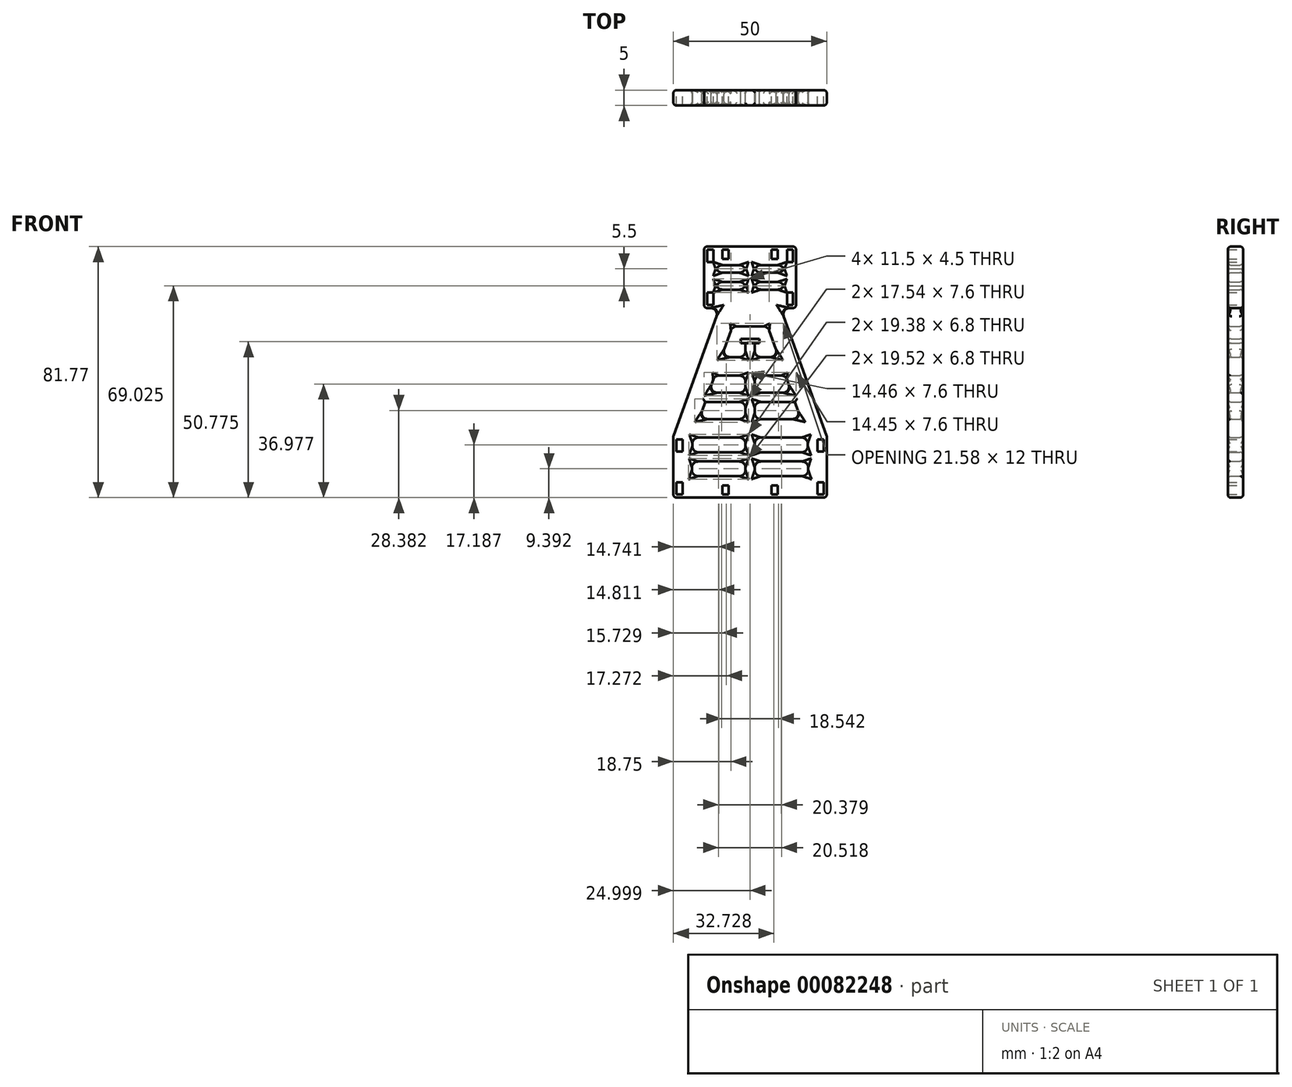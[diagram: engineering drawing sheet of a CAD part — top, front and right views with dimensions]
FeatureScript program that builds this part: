
annotation { "Feature Type Name" : "Feature", "Feature Type Description" : "" }
export const myFeature = defineFeature(function(context is Context, id is Id, definition is map)
    precondition{}
    {
        {
            var Q0;
            Q0=qCreatedBy(makeId("Front.planeOp"),FACE);
            var sketch = newSketch(context, id + "F0", { "sketchPlane" : qUnion([Q0])});
            skLineSegment(sketch, "E0", {"start": v(-24.3, -29.07) * mm, "end": v(-49.3, -29.07) * mm});
            skLineSegment(sketch, "E1", {"start": v(-24.3, -29.07) * mm, "end": v(0.7, -29.07) * mm});
            skLineSegment(sketch, "E2", {"start": v(-49.3, -29.07) * mm, "end": v(-49.3, -9.07) * mm});
            skLineSegment(sketch, "E3", {"start": v(0.7, -29.07) * mm, "end": v(0.7, -9.07) * mm});
            skLineSegment(sketch, "E4", {"start": v(-39.3, 52.7) * mm, "end": v(-39.3, 32.7) * mm});
            skLineSegment(sketch, "E5", {"start": v(-9.3, 52.7) * mm, "end": v(-9.3, 32.7) * mm});
            skLineSegment(sketch, "E6", {"start": v(-39.3, 32.7) * mm, "end": v(-34.3, 32.7) * mm});
            skLineSegment(sketch, "E7", {"start": v(-9.3, 32.7) * mm, "end": v(-14.3, 32.7) * mm});
            skLineSegment(sketch, "E8", {"start": v(-34.3, 32.7) * mm, "end": v(-49.3, -9.07) * mm});
            skLineSegment(sketch, "E9", {"start": v(-14.3, 32.7) * mm, "end": v(0.7, -9.07) * mm});
            skPoint(sketch, "E10.endSnap0", {"position": v(0.7, -19.07) * mm});
            skLineSegment(sketch, "E11", {"start": v(-49.3, -9.07) * mm, "end": v(-49.3, 32.7) * mm});
            skLineSegment(sketch, "E12", {"start": v(0.7, -9.07) * mm, "end": v(0.7, 32.7) * mm});
            skLineSegment(sketch, "E13", {"start": v(-49.3, 11.82) * mm, "end": v(-41.8, 11.82) * mm});
            skLineSegment(sketch, "E14", {"start": v(0.7, 11.82) * mm, "end": v(-6.8, 11.82) * mm});
            skLineSegment(sketch, "E15", {"start": v(-30.08, 26.7) * mm, "end": v(-18.52, 26.7) * mm});
            skLineSegment(sketch, "E16", {"start": v(-39.3, 52.7) * mm, "end": v(-9.3, 52.7) * mm});
            skLineSegment(sketch, "E17", {"start": v(-25.8, 16.7) * mm, "end": v(-25.8, 21.2) * mm});
            skLineSegment(sketch, "E18", {"start": v(-22.8, 16.7) * mm, "end": v(-22.8, 21.2) * mm});
            skLineSegment(sketch, "E19", {"start": v(-27.3, 21.2) * mm, "end": v(-25.8, 21.2) * mm});
            skLineSegment(sketch, "E20", {"start": v(-22.8, 21.2) * mm, "end": v(-21.3, 21.2) * mm});
            skLineSegment(sketch, "E21", {"start": v(-27.3, 21.2) * mm, "end": v(-27.3, 22.7) * mm});
            skLineSegment(sketch, "E22", {"start": v(-21.3, 21.2) * mm, "end": v(-21.3, 22.7) * mm});
            skLineSegment(sketch, "E23", {"start": v(-21.3, 22.7) * mm, "end": v(-27.3, 22.7) * mm});
            skLineSegment(sketch, "E24", {"start": v(-25.8, 10.7) * mm, "end": v(-35.83, 10.7) * mm});
            skLineSegment(sketch, "E25", {"start": v(-22.8, 10.7) * mm, "end": v(-12.78, 10.7) * mm});
            skLineSegment(sketch, "E26", {"start": v(-25.8, -3.49) * mm, "end": v(-40.92, -3.49) * mm});
            skLineSegment(sketch, "E27", {"start": v(-25.8, -9.49) * mm, "end": v(-43.08, -9.49) * mm});
            skLineSegment(sketch, "E28", {"start": v(-22.8, -3.49) * mm, "end": v(-7.68, -3.49) * mm});
            skLineSegment(sketch, "E29", {"start": v(-22.8, -9.49) * mm, "end": v(-5.53, -9.49) * mm});
            skLineSegment(sketch, "E30", {"start": v(-33.67, 16.7) * mm, "end": v(-30.08, 26.7) * mm});
            skLineSegment(sketch, "E31", {"start": v(-18.52, 26.7) * mm, "end": v(-14.93, 16.7) * mm});
            skLineSegment(sketch, "E32", {"start": v(-12.78, 10.7) * mm, "end": v(-7.68, -3.49) * mm});
            skLineSegment(sketch, "E33", {"start": v(-33.67, 16.7) * mm, "end": v(-25.8, 16.7) * mm});
            skLineSegment(sketch, "E34", {"start": v(-22.8, 16.7) * mm, "end": v(-14.93, 16.7) * mm});
            skLineSegment(sketch, "E35", {"start": v(-43.3, -22.08) * mm, "end": v(-25.8, -22.08) * mm});
            skLineSegment(sketch, "E36", {"start": v(-22.8, -22.08) * mm, "end": v(-5.3, -22.08) * mm});
            skLineSegment(sketch, "E37", {"start": v(-35.83, 10.7) * mm, "end": v(-37.83, 5.1) * mm});
            skLineSegment(sketch, "E38", {"start": v(-38.91, 2.1) * mm, "end": v(-40.92, -3.49) * mm});
            skLineSegment(sketch, "E39", {"start": v(-25.8, -3.49) * mm, "end": v(-25.8, 2.1) * mm});
            skLineSegment(sketch, "E40", {"start": v(-25.8, 5.1) * mm, "end": v(-25.8, 10.7) * mm});
            skLineSegment(sketch, "E41", {"start": v(-38.91, 2.1) * mm, "end": v(-25.8, 2.1) * mm});
            skLineSegment(sketch, "E42", {"start": v(-25.8, 5.1) * mm, "end": v(-37.83, 5.1) * mm});
            skLineSegment(sketch, "E43", {"start": v(-22.8, 2.1) * mm, "end": v(-9.69, 2.1) * mm});
            skLineSegment(sketch, "E44", {"start": v(-22.8, 5.1) * mm, "end": v(-10.77, 5.1) * mm});
            skLineSegment(sketch, "E45", {"start": v(-22.8, 10.7) * mm, "end": v(-22.8, 5.1) * mm});
            skLineSegment(sketch, "E46", {"start": v(-22.8, 2.1) * mm, "end": v(-22.8, -3.49) * mm});
            skLineSegment(sketch, "E47", {"start": v(-43.08, -9.49) * mm, "end": v(-43.16, -14.28) * mm});
            skLineSegment(sketch, "E48", {"start": v(-43.22, -17.28) * mm, "end": v(-43.3, -22.08) * mm});
            skLineSegment(sketch, "E49", {"start": v(-25.8, -17.28) * mm, "end": v(-25.8, -22.08) * mm});
            skLineSegment(sketch, "E50", {"start": v(-25.8, -9.49) * mm, "end": v(-25.8, -14.28) * mm});
            skLineSegment(sketch, "E51", {"start": v(-43.16, -14.28) * mm, "end": v(-25.8, -14.28) * mm});
            skLineSegment(sketch, "E52", {"start": v(-25.8, -17.28) * mm, "end": v(-43.22, -17.28) * mm});
            skLineSegment(sketch, "E53", {"start": v(-22.8, -14.28) * mm, "end": v(-5.44, -14.28) * mm});
            skLineSegment(sketch, "E54", {"start": v(-22.8, -17.28) * mm, "end": v(-5.39, -17.28) * mm});
            skLineSegment(sketch, "E55", {"start": v(-22.8, -9.49) * mm, "end": v(-22.8, -14.28) * mm});
            skLineSegment(sketch, "E56", {"start": v(-22.8, -17.28) * mm, "end": v(-22.8, -22.08) * mm});
            skLineSegment(sketch, "E57", {"start": v(-5.3, -22.08) * mm, "end": v(-5.39, -17.28) * mm});
            skLineSegment(sketch, "E58", {"start": v(-5.44, -14.28) * mm, "end": v(-5.53, -9.49) * mm});
            skLineSegment(sketch, "E59", {"start": v(-38.3, 51.7) * mm, "end": v(-36.3, 51.7) * mm});
            skLineSegment(sketch, "E60", {"start": v(-36.3, 33.7) * mm, "end": v(-38.3, 33.7) * mm});
            skLineSegment(sketch, "E61", {"start": v(-38.3, 47.7) * mm, "end": v(-36.3, 47.7) * mm});
            skLineSegment(sketch, "E62", {"start": v(-38.3, 37.7) * mm, "end": v(-36.3, 37.7) * mm});
            skLineSegment(sketch, "E63", {"start": v(-38.3, 51.7) * mm, "end": v(-38.3, 47.7) * mm});
            skLineSegment(sketch, "E64", {"start": v(-36.3, 51.7) * mm, "end": v(-36.3, 47.7) * mm});
            skLineSegment(sketch, "E65", {"start": v(-38.3, 37.7) * mm, "end": v(-38.3, 33.7) * mm});
            skLineSegment(sketch, "E66", {"start": v(-36.3, 37.7) * mm, "end": v(-36.3, 33.7) * mm});
            skLineSegment(sketch, "E67", {"start": v(-12.3, 51.7) * mm, "end": v(-10.3, 51.7) * mm});
            skLineSegment(sketch, "E68", {"start": v(-10.3, 33.7) * mm, "end": v(-12.3, 33.7) * mm});
            skLineSegment(sketch, "E69", {"start": v(-12.3, 47.7) * mm, "end": v(-10.3, 47.7) * mm});
            skLineSegment(sketch, "E70", {"start": v(-12.3, 37.7) * mm, "end": v(-10.3, 37.7) * mm});
            skLineSegment(sketch, "E71", {"start": v(-12.3, 51.7) * mm, "end": v(-12.3, 47.7) * mm});
            skLineSegment(sketch, "E72", {"start": v(-10.3, 51.7) * mm, "end": v(-10.3, 47.7) * mm});
            skLineSegment(sketch, "E73", {"start": v(-12.3, 37.7) * mm, "end": v(-12.3, 33.7) * mm});
            skLineSegment(sketch, "E74", {"start": v(-10.3, 37.7) * mm, "end": v(-10.3, 33.7) * mm});
            skLineSegment(sketch, "E75", {"start": v(-34.3, 32.7) * mm, "end": v(-14.3, 32.7) * mm});
            skLineSegment(sketch, "E76", {"start": v(-35.3, 44.2) * mm, "end": v(-25.8, 44.2) * mm});
            skLineSegment(sketch, "E77", {"start": v(-35.3, 41.2) * mm, "end": v(-25.8, 41.2) * mm});
            skLineSegment(sketch, "E78", {"start": v(-35.3, 46.7) * mm, "end": v(-35.3, 44.2) * mm});
            skLineSegment(sketch, "E79", {"start": v(-35.3, 41.2) * mm, "end": v(-35.3, 38.7) * mm});
            skLineSegment(sketch, "E80", {"start": v(-22.8, 44.2) * mm, "end": v(-13.3, 44.2) * mm});
            skLineSegment(sketch, "E81", {"start": v(-22.8, 41.2) * mm, "end": v(-13.3, 41.2) * mm});
            skLineSegment(sketch, "E82", {"start": v(-35.3, 38.7) * mm, "end": v(-25.8, 38.7) * mm});
            skLineSegment(sketch, "E83", {"start": v(-22.8, 38.7) * mm, "end": v(-13.3, 38.7) * mm});
            skLineSegment(sketch, "E84", {"start": v(-13.3, 46.7) * mm, "end": v(-13.3, 44.2) * mm});
            skLineSegment(sketch, "E85", {"start": v(-13.3, 41.2) * mm, "end": v(-13.3, 38.7) * mm});
            skLineSegment(sketch, "E86", {"start": v(-25.8, 41.2) * mm, "end": v(-25.8, 38.7) * mm});
            skLineSegment(sketch, "E87", {"start": v(-22.8, 41.2) * mm, "end": v(-22.8, 38.7) * mm});
            skLineSegment(sketch, "E88", {"start": v(-25.8, 44.2) * mm, "end": v(-25.8, 46.7) * mm});
            skLineSegment(sketch, "E89", {"start": v(-22.8, 44.2) * mm, "end": v(-22.8, 46.7) * mm});
            skLineSegment(sketch, "E90", {"start": v(-35.3, 46.7) * mm, "end": v(-25.8, 46.7) * mm});
            skLineSegment(sketch, "E91", {"start": v(-22.8, 46.7) * mm, "end": v(-13.3, 46.7) * mm});
            skLineSegment(sketch, "E92", {"start": v(-48.3, -28.07) * mm, "end": v(-46.3, -28.07) * mm});
            skLineSegment(sketch, "E93", {"start": v(-46.3, -10.07) * mm, "end": v(-48.3, -10.07) * mm});
            skLineSegment(sketch, "E94", {"start": v(-48.3, -24.07) * mm, "end": v(-46.3, -24.07) * mm});
            skLineSegment(sketch, "E95", {"start": v(-46.3, -14.07) * mm, "end": v(-48.3, -14.07) * mm});
            skLineSegment(sketch, "E96", {"start": v(-48.3, -10.07) * mm, "end": v(-48.3, -14.07) * mm});
            skLineSegment(sketch, "E97", {"start": v(-46.3, -10.07) * mm, "end": v(-46.3, -14.07) * mm});
            skLineSegment(sketch, "E98", {"start": v(-48.3, -24.07) * mm, "end": v(-48.3, -28.07) * mm});
            skLineSegment(sketch, "E99", {"start": v(-46.3, -24.07) * mm, "end": v(-46.3, -28.07) * mm});
            skLineSegment(sketch, "E100", {"start": v(-0.3, -28.07) * mm, "end": v(-2.3, -28.07) * mm});
            skLineSegment(sketch, "E101", {"start": v(-2.3, -24.07) * mm, "end": v(-2.3, -28.07) * mm});
            skLineSegment(sketch, "E102", {"start": v(-2.3, -24.07) * mm, "end": v(-0.3, -24.07) * mm});
            skLineSegment(sketch, "E103", {"start": v(-0.3, -10.07) * mm, "end": v(-2.3, -10.07) * mm});
            skLineSegment(sketch, "E104", {"start": v(-0.3, -14.07) * mm, "end": v(-2.3, -14.07) * mm});
            skLineSegment(sketch, "E105", {"start": v(-2.3, -14.07) * mm, "end": v(-2.3, -10.07) * mm});
            skLineSegment(sketch, "E106", {"start": v(-0.3, -10.07) * mm, "end": v(-0.3, -14.07) * mm});
            skLineSegment(sketch, "E107", {"start": v(-0.3, -24.07) * mm, "end": v(-0.3, -28.07) * mm});
            skLineSegment(sketch, "E108", {"start": v(-33.3, 51.7) * mm, "end": v(-33.3, 48.7) * mm});
            skLineSegment(sketch, "E109", {"start": v(-33.3, 51.7) * mm, "end": v(-31.3, 51.7) * mm});
            skLineSegment(sketch, "E110", {"start": v(-31.3, 51.7) * mm, "end": v(-31.3, 48.7) * mm});
            skLineSegment(sketch, "E111", {"start": v(-31.3, 48.7) * mm, "end": v(-33.33, 48.71) * mm});
            skLineSegment(sketch, "E112", {"start": v(-15.3, 51.7) * mm, "end": v(-15.3, 48.7) * mm});
            skLineSegment(sketch, "E113", {"start": v(-15.3, 48.7) * mm, "end": v(-17.3, 48.7) * mm});
            skLineSegment(sketch, "E114", {"start": v(-17.3, 48.7) * mm, "end": v(-17.3, 51.7) * mm});
            skLineSegment(sketch, "E115", {"start": v(-17.3, 51.7) * mm, "end": v(-15.3, 51.7) * mm});
            skLineSegment(sketch, "E116", {"start": v(-33.3, -28.07) * mm, "end": v(-31.3, -28.07) * mm});
            skLineSegment(sketch, "E117", {"start": v(-31.3, -28.07) * mm, "end": v(-31.3, -25.07) * mm});
            skLineSegment(sketch, "E118", {"start": v(-31.3, -25.07) * mm, "end": v(-33.3, -25.07) * mm});
            skLineSegment(sketch, "E119", {"start": v(-33.3, -25.07) * mm, "end": v(-33.3, -28.07) * mm});
            skLineSegment(sketch, "E120", {"start": v(-15.3, -28.07) * mm, "end": v(-17.3, -28.07) * mm});
            skLineSegment(sketch, "E121", {"start": v(-17.3, -28.07) * mm, "end": v(-17.3, -25.07) * mm});
            skLineSegment(sketch, "E122", {"start": v(-17.3, -25.07) * mm, "end": v(-15.3, -25.07) * mm});
            skLineSegment(sketch, "E123", {"start": v(-15.3, -25.07) * mm, "end": v(-15.3, -28.07) * mm});
            skLineSegment(sketch, "E124", {"start": v(-46.3, -28.07) * mm, "end": v(-33.3, -28.07) * mm});
            skLineSegment(sketch, "E125", {"start": v(-15.3, -28.07) * mm, "end": v(-2.3, -28.07) * mm});
            skLineSegment(sketch, "E126", {"start": v(-36.3, 51.7) * mm, "end": v(-33.3, 51.7) * mm});
            skLineSegment(sketch, "E127", {"start": v(-15.3, 51.7) * mm, "end": v(-12.3, 51.7) * mm});
            skLineSegment(sketch, "E128", {"start": v(-17.3, -28.07) * mm, "end": v(-31.3, -28.07) * mm});
            skSolve(sketch);
        }
        {
            var Q0;
            Q0=makeQuery(id+"F0.imprint","IMPRINT",FACE,{"disambiguationData":[TD([[makeQuery(id+"F0.imprint","IMPRINT",EDGE,{"derivedFrom":sQuery(id+"F0.wireOp",EDGE,"E0")}),-1.0]])]});
            var Q1;
            {var subQ0=sQuery(id+"F0.wireOp",EDGE,"Gmn1fpuc-x4fh-Dt10-x9JC-7DTWN6bsxrZ6");var subQ3=sQuery(id+"F0.wireOp",EDGE,"DaSBLwFQ-kMCm-d5nd-0PkE-b7sn5duXBcw0");var subQ4=makeQuery(id+"F0.imprint","INTERSECT",VERTEX,{"derivedFrom":[subQ3,subQ0]});Q1=makeQuery(id+"F0.imprint","IMPRINT",FACE,{"disambiguationData":[TD([[makeQuery(id+"F0.imprint","IMPRINT",EDGE,{"disambiguationData":[TD([[subQ4,1.0]])],"derivedFrom":subQ3}),-1.0]])]});}
            var Q2;
            {var subQ0=sQuery(id+"F0.wireOp",EDGE,"E17");Q2=makeQuery(id+"F0.imprint","IMPRINT",FACE,{"disambiguationData":[TD([[makeQuery(id+"F0.imprint","IMPRINT",EDGE,{"derivedFrom":subQ0}),-1.0]])]});}
            var Q3;
            {var subQ0=sQuery(id+"F0.wireOp",EDGE,"Cksz0ew8-7FD8-2HIo-WUUZ-xffdrkzJC516");Q3=makeQuery(id+"F0.imprint","IMPRINT",FACE,{"disambiguationData":[TD([[makeQuery(id+"F0.imprint","IMPRINT",EDGE,{"derivedFrom":subQ0}),-1.0]])]});}
            var Q4;
            {var subQ0=sQuery(id+"F0.wireOp",EDGE,"r91MVb0x-F113-lwMS-o9z4-GQMOX2XZy89u");var subQ3=makeQuery(id+"F0.imprint","INTERSECT",VERTEX,{"derivedFrom":[subQ0,sQuery(id+"F0.wireOp",EDGE,"uLksvqQd-syN0-xw4T-CYru-WyKsU3DyxEXD")]});Q4=makeQuery(id+"F0.imprint","IMPRINT",FACE,{"disambiguationData":[TD([[makeQuery(id+"F0.imprint","IMPRINT",EDGE,{"disambiguationData":[TD([[subQ3,-1.0]])],"derivedFrom":subQ0}),1.0]])]});}
            var Q5;
            {var subQ0=sQuery(id+"F0.wireOp",EDGE,"uLksvqQd-syN0-xw4T-CYru-WyKsU3DyxEXD");Q5=makeQuery(id+"F0.imprint","IMPRINT",FACE,{"disambiguationData":[TD([[makeQuery(id+"F0.imprint","IMPRINT",EDGE,{"derivedFrom":subQ0}),-1.0]])]});}
            var Q6;
            {var subQ0=sQuery(id+"F0.wireOp",EDGE,"E4");Q6=makeQuery(id+"F0.imprint","IMPRINT",FACE,{"disambiguationData":[TD([[makeQuery(id+"F0.imprint","IMPRINT",EDGE,{"derivedFrom":subQ0}),1.0]])]});}
            var Q7;
            {var subQ5=sQuery(id+"F0.wireOp",EDGE,"wKnZqxov-nZ8u-8Se3-picp-5adwDS9QqPhn");Q7=makeQuery(id+"F0.imprint","IMPRINT",FACE,{"disambiguationData":[TD([[makeQuery(id+"F0.imprint","IMPRINT",EDGE,{"derivedFrom":subQ5}),1.0]])]});}
            var Q8;
            {var subQ1=sQuery(id+"F0.wireOp",EDGE,"E5");Q8=makeQuery(id+"F0.imprint","IMPRINT",FACE,{"disambiguationData":[TD([[makeQuery(id+"F0.imprint","IMPRINT",EDGE,{"derivedFrom":subQ1}),-1.0]])]});}
            extrude(context, id + "F1", {"entities" : qUnion([Q0, Q1, Q2, Q3, Q4, Q5, Q6, Q7, Q8]), "depth" : 5 * mm});
        }
        {
            var Q0;
            Q0=makeQuery(id+"F1.opExtrude","CAP_EDGE",EDGE,{"disambiguationData":[OSD([sQuery(id+"F0.wireOp",EDGE,"E2")])],"isStart":false});
            var Q1;
            Q1=makeQuery(id+"F1.opExtrude","CAP_EDGE",EDGE,{"disambiguationData":[OSD([sQuery(id+"F0.wireOp",EDGE,"E0"),sQuery(id+"F0.wireOp",EDGE,"E1")])],"isStart":false});
            var Q2;
            Q2=makeQuery(id+"F1.opExtrude","CAP_EDGE",EDGE,{"disambiguationData":[OSD([sQuery(id+"F0.wireOp",EDGE,"E8")])],"isStart":false});
            var Q3;
            Q3=makeQuery(id+"F1.opExtrude","CAP_EDGE",EDGE,{"disambiguationData":[OSD([sQuery(id+"F0.wireOp",EDGE,"E3")])],"isStart":false});
            var Q4;
            Q4=makeQuery(id+"F1.opExtrude","CAP_EDGE",EDGE,{"disambiguationData":[OSD([sQuery(id+"F0.wireOp",EDGE,"E9")])],"isStart":false});
            var Q5;
            Q5=makeQuery(id+"F1.opExtrude","CAP_EDGE",EDGE,{"disambiguationData":[OSD([sQuery(id+"F0.wireOp",EDGE,"E51")])],"isStart":false});
            var Q6;
            Q6=makeQuery(id+"F1.opExtrude","CAP_EDGE",EDGE,{"disambiguationData":[OSD([sQuery(id+"F0.wireOp",EDGE,"E52")])],"isStart":false});
            var Q7;
            Q7=makeQuery(id+"F1.opExtrude","CAP_EDGE",EDGE,{"disambiguationData":[OSD([sQuery(id+"F0.wireOp",EDGE,"E48")])],"isStart":false});
            var Q8;
            Q8=makeQuery(id+"F1.opExtrude","CAP_EDGE",EDGE,{"disambiguationData":[OSD([sQuery(id+"F0.wireOp",EDGE,"E47")])],"isStart":false});
            var Q9;
            Q9=makeQuery(id+"F1.opExtrude","CAP_EDGE",EDGE,{"disambiguationData":[OSD([sQuery(id+"F0.wireOp",EDGE,"E27")])],"isStart":false});
            var Q10;
            Q10=makeQuery(id+"F1.opExtrude","CAP_EDGE",EDGE,{"disambiguationData":[OSD([sQuery(id+"F0.wireOp",EDGE,"E50")])],"isStart":false});
            var Q11;
            Q11=makeQuery(id+"F1.opExtrude","CAP_EDGE",EDGE,{"disambiguationData":[OSD([sQuery(id+"F0.wireOp",EDGE,"E35")])],"isStart":false});
            var Q12;
            Q12=makeQuery(id+"F1.opExtrude","CAP_EDGE",EDGE,{"disambiguationData":[OSD([sQuery(id+"F0.wireOp",EDGE,"E49")])],"isStart":false});
            var Q13;
            Q13=makeQuery(id+"F1.opExtrude","CAP_EDGE",EDGE,{"disambiguationData":[OSD([sQuery(id+"F0.wireOp",EDGE,"E36")])],"isStart":false});
            var Q14;
            Q14=makeQuery(id+"F1.opExtrude","CAP_EDGE",EDGE,{"disambiguationData":[OSD([sQuery(id+"F0.wireOp",EDGE,"E56")])],"isStart":false});
            var Q15;
            Q15=makeQuery(id+"F1.opExtrude","CAP_EDGE",EDGE,{"disambiguationData":[OSD([sQuery(id+"F0.wireOp",EDGE,"E54")])],"isStart":false});
            var Q16;
            Q16=makeQuery(id+"F1.opExtrude","CAP_EDGE",EDGE,{"disambiguationData":[OSD([sQuery(id+"F0.wireOp",EDGE,"E57")])],"isStart":false});
            var Q17;
            Q17=makeQuery(id+"F1.opExtrude","CAP_EDGE",EDGE,{"disambiguationData":[OSD([sQuery(id+"F0.wireOp",EDGE,"E29")])],"isStart":false});
            var Q18;
            Q18=makeQuery(id+"F1.opExtrude","CAP_EDGE",EDGE,{"disambiguationData":[OSD([sQuery(id+"F0.wireOp",EDGE,"E55")])],"isStart":false});
            var Q19;
            Q19=makeQuery(id+"F1.opExtrude","CAP_EDGE",EDGE,{"disambiguationData":[OSD([sQuery(id+"F0.wireOp",EDGE,"E58")])],"isStart":false});
            var Q20;
            Q20=makeQuery(id+"F1.opExtrude","CAP_EDGE",EDGE,{"disambiguationData":[OSD([sQuery(id+"F0.wireOp",EDGE,"E38")])],"isStart":false});
            var Q21;
            Q21=makeQuery(id+"F1.opExtrude","CAP_EDGE",EDGE,{"disambiguationData":[OSD([sQuery(id+"F0.wireOp",EDGE,"E26")])],"isStart":false});
            var Q22;
            Q22=makeQuery(id+"F1.opExtrude","CAP_EDGE",EDGE,{"disambiguationData":[OSD([sQuery(id+"F0.wireOp",EDGE,"E41")])],"isStart":false});
            var Q23;
            Q23=makeQuery(id+"F1.opExtrude","CAP_EDGE",EDGE,{"disambiguationData":[OSD([sQuery(id+"F0.wireOp",EDGE,"E39")])],"isStart":false});
            var Q24;
            Q24=makeQuery(id+"F1.opExtrude","CAP_EDGE",EDGE,{"disambiguationData":[OSD([sQuery(id+"F0.wireOp",EDGE,"E46")])],"isStart":false});
            var Q25;
            Q25=makeQuery(id+"F1.opExtrude","CAP_EDGE",EDGE,{"disambiguationData":[OSD([sQuery(id+"F0.wireOp",EDGE,"E43")])],"isStart":false});
            var Q26;
            {var subQ0=sQuery(id+"F0.wireOp",EDGE,"E32");Q26=makeQuery(id+"F1.opExtrude","CAP_EDGE",EDGE,{"disambiguationData":[OSD([subQ0]),TDD([makeQuery(id+"F0.imprint","IMPRINT",EDGE,{"disambiguationData":[TD([[makeQuery(id+"F0.imprint","INTERSECT",VERTEX,{"derivedFrom":[sQuery(id+"F0.wireOp",EDGE,"E28"),subQ0]}),1.0]])],"derivedFrom":subQ0})])],"isStart":false});}
            var Q27;
            Q27=makeQuery(id+"F1.opExtrude","CAP_EDGE",EDGE,{"disambiguationData":[OSD([sQuery(id+"F0.wireOp",EDGE,"E28")])],"isStart":false});
            var Q28;
            Q28=makeQuery(id+"F1.opExtrude","CAP_EDGE",EDGE,{"disambiguationData":[OSD([sQuery(id+"F0.wireOp",EDGE,"E45")])],"isStart":false});
            var Q29;
            Q29=makeQuery(id+"F1.opExtrude","CAP_EDGE",EDGE,{"disambiguationData":[OSD([sQuery(id+"F0.wireOp",EDGE,"E44")])],"isStart":false});
            var Q30;
            Q30=makeQuery(id+"F1.opExtrude","CAP_EDGE",EDGE,{"disambiguationData":[OSD([sQuery(id+"F0.wireOp",EDGE,"E25")])],"isStart":false});
            var Q31;
            {var subQ0=sQuery(id+"F0.wireOp",EDGE,"E32");Q31=makeQuery(id+"F1.opExtrude","CAP_EDGE",EDGE,{"disambiguationData":[OSD([subQ0]),TDD([makeQuery(id+"F0.imprint","IMPRINT",EDGE,{"disambiguationData":[TD([[makeQuery(id+"F0.imprint","INTERSECT",VERTEX,{"derivedFrom":[sQuery(id+"F0.wireOp",EDGE,"E25"),subQ0]}),-1.0]])],"derivedFrom":subQ0})])],"isStart":false});}
            var Q32;
            Q32=makeQuery(id+"F1.opExtrude","CAP_EDGE",EDGE,{"disambiguationData":[OSD([sQuery(id+"F0.wireOp",EDGE,"E42")])],"isStart":false});
            var Q33;
            Q33=makeQuery(id+"F1.opExtrude","CAP_EDGE",EDGE,{"disambiguationData":[OSD([sQuery(id+"F0.wireOp",EDGE,"E37")])],"isStart":false});
            var Q34;
            Q34=makeQuery(id+"F1.opExtrude","CAP_EDGE",EDGE,{"disambiguationData":[OSD([sQuery(id+"F0.wireOp",EDGE,"E24")])],"isStart":false});
            var Q35;
            Q35=makeQuery(id+"F1.opExtrude","CAP_EDGE",EDGE,{"disambiguationData":[OSD([sQuery(id+"F0.wireOp",EDGE,"E40")])],"isStart":false});
            var Q36;
            Q36=makeQuery(id+"F1.opExtrude","CAP_EDGE",EDGE,{"disambiguationData":[OSD([sQuery(id+"F0.wireOp",EDGE,"E33")])],"isStart":false});
            var Q37;
            Q37=makeQuery(id+"F1.opExtrude","CAP_EDGE",EDGE,{"disambiguationData":[OSD([sQuery(id+"F0.wireOp",EDGE,"E30")])],"isStart":false});
            var Q38;
            Q38=makeQuery(id+"F1.opExtrude","CAP_EDGE",EDGE,{"disambiguationData":[OSD([sQuery(id+"F0.wireOp",EDGE,"E15")])],"isStart":false});
            var Q39;
            Q39=makeQuery(id+"F1.opExtrude","CAP_EDGE",EDGE,{"disambiguationData":[OSD([sQuery(id+"F0.wireOp",EDGE,"E31")])],"isStart":false});
            var Q40;
            Q40=makeQuery(id+"F1.opExtrude","CAP_EDGE",EDGE,{"disambiguationData":[OSD([sQuery(id+"F0.wireOp",EDGE,"E34")])],"isStart":false});
            var Q41;
            Q41=makeQuery(id+"F1.opExtrude","CAP_EDGE",EDGE,{"disambiguationData":[OSD([sQuery(id+"F0.wireOp",EDGE,"E17")])],"isStart":false});
            var Q42;
            Q42=makeQuery(id+"F1.opExtrude","CAP_EDGE",EDGE,{"disambiguationData":[OSD([sQuery(id+"F0.wireOp",EDGE,"E18")])],"isStart":false});
            var Q43;
            Q43=makeQuery(id+"F1.opExtrude","CAP_EDGE",EDGE,{"disambiguationData":[OSD([sQuery(id+"F0.wireOp",EDGE,"E6")])],"isStart":false});
            var Q44;
            Q44=makeQuery(id+"F1.opExtrude","CAP_EDGE",EDGE,{"disambiguationData":[OSD([sQuery(id+"F0.wireOp",EDGE,"E4")])],"isStart":false});
            var Q45;
            Q45=makeQuery(id+"F1.opExtrude","CAP_EDGE",EDGE,{"disambiguationData":[OSD([sQuery(id+"F0.wireOp",EDGE,"E16")])],"isStart":false});
            var Q46;
            Q46=makeQuery(id+"F1.opExtrude","CAP_EDGE",EDGE,{"disambiguationData":[OSD([sQuery(id+"F0.wireOp",EDGE,"E5")])],"isStart":false});
            var Q47;
            Q47=makeQuery(id+"F1.opExtrude","CAP_EDGE",EDGE,{"disambiguationData":[OSD([sQuery(id+"F0.wireOp",EDGE,"E7")])],"isStart":false});
            var Q48;
            Q48=makeQuery(id+"F1.opExtrude","CAP_EDGE",EDGE,{"disambiguationData":[OSD([sQuery(id+"F0.wireOp",EDGE,"ymKoGDRe-bliB-sY5n-xFfI-t996A0unm5Td")])],"isStart":false});
            var Q49;
            Q49=makeQuery(id+"F1.opExtrude","CAP_EDGE",EDGE,{"disambiguationData":[OSD([sQuery(id+"F0.wireOp",EDGE,"wKnZqxov-nZ8u-8Se3-picp-5adwDS9QqPhn")])],"isStart":false});
            var Q50;
            Q50=makeQuery(id+"F1.opExtrude","CAP_EDGE",EDGE,{"disambiguationData":[OSD([sQuery(id+"F0.wireOp",EDGE,"p78FREQm-4KwS-vw5M-QSKw-gRrmDGhDhAHL")])],"isStart":false});
            var Q51;
            Q51=makeQuery(id+"F1.opExtrude","CAP_EDGE",EDGE,{"disambiguationData":[OSD([sQuery(id+"F0.wireOp",EDGE,"E76")])],"isStart":false});
            var Q52;
            Q52=makeQuery(id+"F1.opExtrude","CAP_EDGE",EDGE,{"disambiguationData":[OSD([sQuery(id+"F0.wireOp",EDGE,"E78")])],"isStart":false});
            var Q53;
            Q53=makeQuery(id+"F1.opExtrude","CAP_EDGE",EDGE,{"disambiguationData":[OSD([sQuery(id+"F0.wireOp",EDGE,"E90")])],"isStart":false});
            var Q54;
            Q54=makeQuery(id+"F1.opExtrude","CAP_EDGE",EDGE,{"disambiguationData":[OSD([sQuery(id+"F0.wireOp",EDGE,"E88")])],"isStart":false});
            var Q55;
            Q55=makeQuery(id+"F1.opExtrude","CAP_EDGE",EDGE,{"disambiguationData":[OSD([sQuery(id+"F0.wireOp",EDGE,"E80")])],"isStart":false});
            var Q56;
            Q56=makeQuery(id+"F1.opExtrude","CAP_EDGE",EDGE,{"disambiguationData":[OSD([sQuery(id+"F0.wireOp",EDGE,"E91")])],"isStart":false});
            var Q57;
            Q57=makeQuery(id+"F1.opExtrude","CAP_EDGE",EDGE,{"disambiguationData":[OSD([sQuery(id+"F0.wireOp",EDGE,"E89")])],"isStart":false});
            var Q58;
            Q58=makeQuery(id+"F1.opExtrude","CAP_EDGE",EDGE,{"disambiguationData":[OSD([sQuery(id+"F0.wireOp",EDGE,"E84")])],"isStart":false});
            var Q59;
            Q59=makeQuery(id+"F1.opExtrude","CAP_EDGE",EDGE,{"disambiguationData":[OSD([sQuery(id+"F0.wireOp",EDGE,"E87")])],"isStart":false});
            var Q60;
            Q60=makeQuery(id+"F1.opExtrude","CAP_EDGE",EDGE,{"disambiguationData":[OSD([sQuery(id+"F0.wireOp",EDGE,"E81")])],"isStart":false});
            var Q61;
            Q61=makeQuery(id+"F1.opExtrude","CAP_EDGE",EDGE,{"disambiguationData":[OSD([sQuery(id+"F0.wireOp",EDGE,"E85")])],"isStart":false});
            var Q62;
            Q62=makeQuery(id+"F1.opExtrude","CAP_EDGE",EDGE,{"disambiguationData":[OSD([sQuery(id+"F0.wireOp",EDGE,"E83")])],"isStart":false});
            var Q63;
            Q63=makeQuery(id+"F1.opExtrude","CAP_EDGE",EDGE,{"disambiguationData":[OSD([sQuery(id+"F0.wireOp",EDGE,"E77")])],"isStart":false});
            var Q64;
            Q64=makeQuery(id+"F1.opExtrude","CAP_EDGE",EDGE,{"disambiguationData":[OSD([sQuery(id+"F0.wireOp",EDGE,"E79")])],"isStart":false});
            var Q65;
            Q65=makeQuery(id+"F1.opExtrude","CAP_EDGE",EDGE,{"disambiguationData":[OSD([sQuery(id+"F0.wireOp",EDGE,"E82")])],"isStart":false});
            var Q66;
            Q66=makeQuery(id+"F1.opExtrude","CAP_EDGE",EDGE,{"disambiguationData":[OSD([sQuery(id+"F0.wireOp",EDGE,"E86")])],"isStart":false});
            var Q67;
            Q67=makeQuery(id+"F1.opExtrude","CAP_EDGE",EDGE,{"disambiguationData":[OSD([sQuery(id+"F0.wireOp",EDGE,"E53")])],"isStart":false});
            var Q68;
            Q68=makeQuery(id+"F1.opExtrude","SWEPT_EDGE",EDGE,{"disambiguationData":[OSD([sQuery(id+"F0.wireOp",EDGE,"E2"),sQuery(id+"F0.wireOp",EDGE,"E8"),sQuery(id+"F0.wireOp",EDGE,"E11")])]});
            var Q69;
            Q69=makeQuery(id+"F1.opExtrude","SWEPT_EDGE",EDGE,{"disambiguationData":[OSD([sQuery(id+"F0.wireOp",EDGE,"E4"),sQuery(id+"F0.wireOp",EDGE,"E6")])]});
            var Q70;
            Q70=makeQuery(id+"F1.opExtrude","SWEPT_EDGE",EDGE,{"disambiguationData":[OSD([sQuery(id+"F0.wireOp",EDGE,"E0"),sQuery(id+"F0.wireOp",EDGE,"E2")])]});
            var Q71;
            Q71=makeQuery(id+"F1.opExtrude","SWEPT_EDGE",EDGE,{"disambiguationData":[OSD([sQuery(id+"F0.wireOp",EDGE,"E4"),sQuery(id+"F0.wireOp",EDGE,"E16")])]});
            var Q72;
            Q72=makeQuery(id+"F1.opExtrude","SWEPT_EDGE",EDGE,{"disambiguationData":[OSD([sQuery(id+"F0.wireOp",EDGE,"E3"),sQuery(id+"F0.wireOp",EDGE,"E9"),sQuery(id+"F0.wireOp",EDGE,"E12")])]});
            var Q73;
            Q73=makeQuery(id+"F1.opExtrude","SWEPT_EDGE",EDGE,{"disambiguationData":[OSD([sQuery(id+"F0.wireOp",EDGE,"E5"),sQuery(id+"F0.wireOp",EDGE,"E16")])]});
            var Q74;
            Q74=makeQuery(id+"F1.opExtrude","SWEPT_EDGE",EDGE,{"disambiguationData":[OSD([sQuery(id+"F0.wireOp",EDGE,"E5"),sQuery(id+"F0.wireOp",EDGE,"E7")])]});
            var Q75;
            Q75=makeQuery(id+"F1.opExtrude","SWEPT_EDGE",EDGE,{"disambiguationData":[OSD([sQuery(id+"F0.wireOp",EDGE,"E1"),sQuery(id+"F0.wireOp",EDGE,"E3")])]});
            fillet(context, id + "F2", {"entities" : qUnion([Q0, Q1, Q2, Q3, Q4, Q5, Q6, Q7, Q8, Q9, Q10, Q11, Q12, Q13, Q14, Q15, Q16, Q17, Q18, Q19, Q20, Q21, Q22, Q23, Q24, Q25, Q26, Q27, Q28, Q29, Q30, Q31, Q32, Q33, Q34, Q35, Q36, Q37, Q38, Q39, Q40, Q41, Q42, Q43, Q44, Q45, Q46, Q47, Q48, Q49, Q50, Q51, Q52, Q53, Q54, Q55, Q56, Q57, Q58, Q59, Q60, Q61, Q62, Q63, Q64, Q65, Q66, Q67, Q68, Q69, Q70, Q71, Q72, Q73, Q74, Q75]), "radius" : 1 * mm, "tangentPropagation" : true, "allowEdgeOverflow" : false});
        }
        {
            var Q0;
            Q0=makeQuery(id+"F1.opExtrude","CAP_EDGE",EDGE,{"disambiguationData":[OSD([sQuery(id+"F0.wireOp",EDGE,"E16")])],"isStart":true});
            var Q1;
            Q1=makeQuery(id+"F1.opExtrude","CAP_EDGE",EDGE,{"disambiguationData":[OSD([sQuery(id+"F0.wireOp",EDGE,"E5")])],"isStart":true});
            var Q2;
            Q2=makeQuery(id+"F1.opExtrude","CAP_EDGE",EDGE,{"disambiguationData":[OSD([sQuery(id+"F0.wireOp",EDGE,"E4")])],"isStart":true});
            var Q3;
            Q3=makeQuery(id+"F1.opExtrude","CAP_EDGE",EDGE,{"disambiguationData":[OSD([sQuery(id+"F0.wireOp",EDGE,"E6")])],"isStart":true});
            var Q4;
            Q4=makeQuery(id+"F1.opExtrude","CAP_EDGE",EDGE,{"disambiguationData":[OSD([sQuery(id+"F0.wireOp",EDGE,"E7")])],"isStart":true});
            var Q5;
            Q5=makeQuery(id+"F1.opExtrude","CAP_EDGE",EDGE,{"disambiguationData":[OSD([sQuery(id+"F0.wireOp",EDGE,"E9")])],"isStart":true});
            var Q6;
            Q6=makeQuery(id+"F1.opExtrude","CAP_EDGE",EDGE,{"disambiguationData":[OSD([sQuery(id+"F0.wireOp",EDGE,"E8")])],"isStart":true});
            var Q7;
            Q7=makeQuery(id+"F1.opExtrude","CAP_EDGE",EDGE,{"disambiguationData":[OSD([sQuery(id+"F0.wireOp",EDGE,"E33")])],"isStart":true});
            var Q8;
            Q8=makeQuery(id+"F1.opExtrude","CAP_EDGE",EDGE,{"disambiguationData":[OSD([sQuery(id+"F0.wireOp",EDGE,"E17")])],"isStart":true});
            var Q9;
            Q9=makeQuery(id+"F1.opExtrude","CAP_EDGE",EDGE,{"disambiguationData":[OSD([sQuery(id+"F0.wireOp",EDGE,"E18")])],"isStart":true});
            var Q10;
            Q10=makeQuery(id+"F1.opExtrude","CAP_EDGE",EDGE,{"disambiguationData":[OSD([sQuery(id+"F0.wireOp",EDGE,"E34")])],"isStart":true});
            var Q11;
            Q11=makeQuery(id+"F1.opExtrude","CAP_EDGE",EDGE,{"disambiguationData":[OSD([sQuery(id+"F0.wireOp",EDGE,"E31")])],"isStart":true});
            var Q12;
            Q12=makeQuery(id+"F1.opExtrude","CAP_EDGE",EDGE,{"disambiguationData":[OSD([sQuery(id+"F0.wireOp",EDGE,"E15")])],"isStart":true});
            var Q13;
            Q13=makeQuery(id+"F1.opExtrude","CAP_EDGE",EDGE,{"disambiguationData":[OSD([sQuery(id+"F0.wireOp",EDGE,"E30")])],"isStart":true});
            var Q14;
            Q14=makeQuery(id+"F1.opExtrude","CAP_EDGE",EDGE,{"disambiguationData":[OSD([sQuery(id+"F0.wireOp",EDGE,"E25")])],"isStart":true});
            var Q15;
            {var subQ0=sQuery(id+"F0.wireOp",EDGE,"E32");Q15=makeQuery(id+"F1.opExtrude","CAP_EDGE",EDGE,{"disambiguationData":[OSD([subQ0]),TDD([makeQuery(id+"F0.imprint","IMPRINT",EDGE,{"disambiguationData":[TD([[makeQuery(id+"F0.imprint","INTERSECT",VERTEX,{"derivedFrom":[sQuery(id+"F0.wireOp",EDGE,"E25"),subQ0]}),-1.0]])],"derivedFrom":subQ0})])],"isStart":true});}
            var Q16;
            Q16=makeQuery(id+"F1.opExtrude","CAP_EDGE",EDGE,{"disambiguationData":[OSD([sQuery(id+"F0.wireOp",EDGE,"E44")])],"isStart":true});
            var Q17;
            Q17=makeQuery(id+"F1.opExtrude","CAP_EDGE",EDGE,{"disambiguationData":[OSD([sQuery(id+"F0.wireOp",EDGE,"E45")])],"isStart":true});
            var Q18;
            Q18=makeQuery(id+"F1.opExtrude","CAP_EDGE",EDGE,{"disambiguationData":[OSD([sQuery(id+"F0.wireOp",EDGE,"E40")])],"isStart":true});
            var Q19;
            Q19=makeQuery(id+"F1.opExtrude","CAP_EDGE",EDGE,{"disambiguationData":[OSD([sQuery(id+"F0.wireOp",EDGE,"E24")])],"isStart":true});
            var Q20;
            Q20=makeQuery(id+"F1.opExtrude","CAP_EDGE",EDGE,{"disambiguationData":[OSD([sQuery(id+"F0.wireOp",EDGE,"E37")])],"isStart":true});
            var Q21;
            Q21=makeQuery(id+"F1.opExtrude","CAP_EDGE",EDGE,{"disambiguationData":[OSD([sQuery(id+"F0.wireOp",EDGE,"E42")])],"isStart":true});
            var Q22;
            Q22=makeQuery(id+"F1.opExtrude","CAP_EDGE",EDGE,{"disambiguationData":[OSD([sQuery(id+"F0.wireOp",EDGE,"E43")])],"isStart":true});
            var Q23;
            {var subQ0=sQuery(id+"F0.wireOp",EDGE,"E32");Q23=makeQuery(id+"F1.opExtrude","CAP_EDGE",EDGE,{"disambiguationData":[OSD([subQ0]),TDD([makeQuery(id+"F0.imprint","IMPRINT",EDGE,{"disambiguationData":[TD([[makeQuery(id+"F0.imprint","INTERSECT",VERTEX,{"derivedFrom":[sQuery(id+"F0.wireOp",EDGE,"E28"),subQ0]}),1.0]])],"derivedFrom":subQ0})])],"isStart":true});}
            var Q24;
            Q24=makeQuery(id+"F1.opExtrude","CAP_EDGE",EDGE,{"disambiguationData":[OSD([sQuery(id+"F0.wireOp",EDGE,"E28")])],"isStart":true});
            var Q25;
            Q25=makeQuery(id+"F1.opExtrude","CAP_EDGE",EDGE,{"disambiguationData":[OSD([sQuery(id+"F0.wireOp",EDGE,"E46")])],"isStart":true});
            var Q26;
            Q26=makeQuery(id+"F1.opExtrude","CAP_EDGE",EDGE,{"disambiguationData":[OSD([sQuery(id+"F0.wireOp",EDGE,"E26")])],"isStart":true});
            var Q27;
            Q27=makeQuery(id+"F1.opExtrude","CAP_EDGE",EDGE,{"disambiguationData":[OSD([sQuery(id+"F0.wireOp",EDGE,"E41")])],"isStart":true});
            var Q28;
            Q28=makeQuery(id+"F1.opExtrude","CAP_EDGE",EDGE,{"disambiguationData":[OSD([sQuery(id+"F0.wireOp",EDGE,"E38")])],"isStart":true});
            var Q29;
            Q29=makeQuery(id+"F1.opExtrude","CAP_EDGE",EDGE,{"disambiguationData":[OSD([sQuery(id+"F0.wireOp",EDGE,"E39")])],"isStart":true});
            var Q30;
            Q30=makeQuery(id+"F1.opExtrude","CAP_EDGE",EDGE,{"disambiguationData":[OSD([sQuery(id+"F0.wireOp",EDGE,"E27")])],"isStart":true});
            var Q31;
            Q31=makeQuery(id+"F1.opExtrude","CAP_EDGE",EDGE,{"disambiguationData":[OSD([sQuery(id+"F0.wireOp",EDGE,"E50")])],"isStart":true});
            var Q32;
            Q32=makeQuery(id+"F1.opExtrude","CAP_EDGE",EDGE,{"disambiguationData":[OSD([sQuery(id+"F0.wireOp",EDGE,"E52")])],"isStart":true});
            var Q33;
            Q33=makeQuery(id+"F1.opExtrude","CAP_EDGE",EDGE,{"disambiguationData":[OSD([sQuery(id+"F0.wireOp",EDGE,"E51")])],"isStart":true});
            var Q34;
            Q34=makeQuery(id+"F1.opExtrude","CAP_EDGE",EDGE,{"disambiguationData":[OSD([sQuery(id+"F0.wireOp",EDGE,"E47")])],"isStart":true});
            var Q35;
            Q35=makeQuery(id+"F1.opExtrude","CAP_EDGE",EDGE,{"disambiguationData":[OSD([sQuery(id+"F0.wireOp",EDGE,"E48")])],"isStart":true});
            var Q36;
            Q36=makeQuery(id+"F1.opExtrude","CAP_EDGE",EDGE,{"disambiguationData":[OSD([sQuery(id+"F0.wireOp",EDGE,"E35")])],"isStart":true});
            var Q37;
            Q37=makeQuery(id+"F1.opExtrude","CAP_EDGE",EDGE,{"disambiguationData":[OSD([sQuery(id+"F0.wireOp",EDGE,"E49")])],"isStart":true});
            var Q38;
            Q38=makeQuery(id+"F1.opExtrude","CAP_EDGE",EDGE,{"disambiguationData":[OSD([sQuery(id+"F0.wireOp",EDGE,"E55")])],"isStart":true});
            var Q39;
            Q39=makeQuery(id+"F1.opExtrude","CAP_EDGE",EDGE,{"disambiguationData":[OSD([sQuery(id+"F0.wireOp",EDGE,"E29")])],"isStart":true});
            var Q40;
            Q40=makeQuery(id+"F1.opExtrude","CAP_EDGE",EDGE,{"disambiguationData":[OSD([sQuery(id+"F0.wireOp",EDGE,"E58")])],"isStart":true});
            var Q41;
            Q41=makeQuery(id+"F1.opExtrude","CAP_EDGE",EDGE,{"disambiguationData":[OSD([sQuery(id+"F0.wireOp",EDGE,"E53")])],"isStart":true});
            var Q42;
            Q42=makeQuery(id+"F1.opExtrude","CAP_EDGE",EDGE,{"disambiguationData":[OSD([sQuery(id+"F0.wireOp",EDGE,"E54")])],"isStart":true});
            var Q43;
            Q43=makeQuery(id+"F1.opExtrude","CAP_EDGE",EDGE,{"disambiguationData":[OSD([sQuery(id+"F0.wireOp",EDGE,"E57")])],"isStart":true});
            var Q44;
            Q44=makeQuery(id+"F1.opExtrude","CAP_EDGE",EDGE,{"disambiguationData":[OSD([sQuery(id+"F0.wireOp",EDGE,"E36")])],"isStart":true});
            var Q45;
            Q45=makeQuery(id+"F1.opExtrude","CAP_EDGE",EDGE,{"disambiguationData":[OSD([sQuery(id+"F0.wireOp",EDGE,"E56")])],"isStart":true});
            var Q46;
            Q46=makeQuery(id+"F1.opExtrude","CAP_EDGE",EDGE,{"disambiguationData":[OSD([sQuery(id+"F0.wireOp",EDGE,"E3")])],"isStart":true});
            var Q47;
            Q47=makeQuery(id+"F1.opExtrude","CAP_EDGE",EDGE,{"disambiguationData":[OSD([sQuery(id+"F0.wireOp",EDGE,"E2")])],"isStart":true});
            var Q48;
            Q48=makeQuery(id+"F1.opExtrude","CAP_EDGE",EDGE,{"disambiguationData":[OSD([sQuery(id+"F0.wireOp",EDGE,"E0"),sQuery(id+"F0.wireOp",EDGE,"E1")])],"isStart":true});
            var Q49;
            Q49=makeQuery(id+"F1.opExtrude","CAP_EDGE",EDGE,{"disambiguationData":[OSD([sQuery(id+"F0.wireOp",EDGE,"p78FREQm-4KwS-vw5M-QSKw-gRrmDGhDhAHL")])],"isStart":true});
            var Q50;
            Q50=makeQuery(id+"F1.opExtrude","CAP_EDGE",EDGE,{"disambiguationData":[OSD([sQuery(id+"F0.wireOp",EDGE,"wKnZqxov-nZ8u-8Se3-picp-5adwDS9QqPhn")])],"isStart":true});
            var Q51;
            Q51=makeQuery(id+"F1.opExtrude","CAP_EDGE",EDGE,{"disambiguationData":[OSD([sQuery(id+"F0.wireOp",EDGE,"ymKoGDRe-bliB-sY5n-xFfI-t996A0unm5Td")])],"isStart":true});
            var Q52;
            Q52=makeQuery(id+"F1.opExtrude","CAP_EDGE",EDGE,{"disambiguationData":[OSD([sQuery(id+"F0.wireOp",EDGE,"E23")])],"isStart":true});
            var Q53;
            Q53=makeQuery(id+"F1.opExtrude","CAP_EDGE",EDGE,{"disambiguationData":[OSD([sQuery(id+"F0.wireOp",EDGE,"E23")])],"isStart":false});
            var Q54;
            Q54=makeQuery(id+"F1.opExtrude","CAP_EDGE",EDGE,{"disambiguationData":[OSD([sQuery(id+"F0.wireOp",EDGE,"E81")])],"isStart":true});
            var Q55;
            Q55=makeQuery(id+"F1.opExtrude","CAP_EDGE",EDGE,{"disambiguationData":[OSD([sQuery(id+"F0.wireOp",EDGE,"E85")])],"isStart":true});
            var Q56;
            Q56=makeQuery(id+"F1.opExtrude","CAP_EDGE",EDGE,{"disambiguationData":[OSD([sQuery(id+"F0.wireOp",EDGE,"E83")])],"isStart":true});
            var Q57;
            Q57=makeQuery(id+"F1.opExtrude","CAP_EDGE",EDGE,{"disambiguationData":[OSD([sQuery(id+"F0.wireOp",EDGE,"E87")])],"isStart":true});
            var Q58;
            Q58=makeQuery(id+"F1.opExtrude","CAP_EDGE",EDGE,{"disambiguationData":[OSD([sQuery(id+"F0.wireOp",EDGE,"E91")])],"isStart":true});
            var Q59;
            Q59=makeQuery(id+"F1.opExtrude","CAP_EDGE",EDGE,{"disambiguationData":[OSD([sQuery(id+"F0.wireOp",EDGE,"E84")])],"isStart":true});
            var Q60;
            Q60=makeQuery(id+"F1.opExtrude","CAP_EDGE",EDGE,{"disambiguationData":[OSD([sQuery(id+"F0.wireOp",EDGE,"E80")])],"isStart":true});
            var Q61;
            Q61=makeQuery(id+"F1.opExtrude","CAP_EDGE",EDGE,{"disambiguationData":[OSD([sQuery(id+"F0.wireOp",EDGE,"E89")])],"isStart":true});
            var Q62;
            Q62=makeQuery(id+"F1.opExtrude","CAP_EDGE",EDGE,{"disambiguationData":[OSD([sQuery(id+"F0.wireOp",EDGE,"E90")])],"isStart":true});
            var Q63;
            Q63=makeQuery(id+"F1.opExtrude","CAP_EDGE",EDGE,{"disambiguationData":[OSD([sQuery(id+"F0.wireOp",EDGE,"E88")])],"isStart":true});
            var Q64;
            Q64=makeQuery(id+"F1.opExtrude","CAP_EDGE",EDGE,{"disambiguationData":[OSD([sQuery(id+"F0.wireOp",EDGE,"E76")])],"isStart":true});
            var Q65;
            Q65=makeQuery(id+"F1.opExtrude","CAP_EDGE",EDGE,{"disambiguationData":[OSD([sQuery(id+"F0.wireOp",EDGE,"E78")])],"isStart":true});
            var Q66;
            Q66=makeQuery(id+"F1.opExtrude","CAP_EDGE",EDGE,{"disambiguationData":[OSD([sQuery(id+"F0.wireOp",EDGE,"E77")])],"isStart":true});
            var Q67;
            Q67=makeQuery(id+"F1.opExtrude","CAP_EDGE",EDGE,{"disambiguationData":[OSD([sQuery(id+"F0.wireOp",EDGE,"E86")])],"isStart":true});
            var Q68;
            Q68=makeQuery(id+"F1.opExtrude","CAP_EDGE",EDGE,{"disambiguationData":[OSD([sQuery(id+"F0.wireOp",EDGE,"E82")])],"isStart":true});
            var Q69;
            Q69=makeQuery(id+"F1.opExtrude","CAP_EDGE",EDGE,{"disambiguationData":[OSD([sQuery(id+"F0.wireOp",EDGE,"E79")])],"isStart":true});
            fillet(context, id + "F3", {"entities" : qUnion([Q0, Q1, Q2, Q3, Q4, Q5, Q6, Q7, Q8, Q9, Q10, Q11, Q12, Q13, Q14, Q15, Q16, Q17, Q18, Q19, Q20, Q21, Q22, Q23, Q24, Q25, Q26, Q27, Q28, Q29, Q30, Q31, Q32, Q33, Q34, Q35, Q36, Q37, Q38, Q39, Q40, Q41, Q42, Q43, Q44, Q45, Q46, Q47, Q48, Q49, Q50, Q51, Q52, Q53, Q54, Q55, Q56, Q57, Q58, Q59, Q60, Q61, Q62, Q63, Q64, Q65, Q66, Q67, Q68, Q69]), "radius" : 1 * mm, "tangentPropagation" : true, "allowEdgeOverflow" : false});
        }
        {
            var Q0;
            Q0=makeQuery(id+"F1.opExtrude","SWEPT_EDGE",EDGE,{"disambiguationData":[OSD([sQuery(id+"F0.wireOp",EDGE,"E6"),sQuery(id+"F0.wireOp",EDGE,"E8"),sQuery(id+"F0.wireOp",EDGE,"E75")])]});
            var Q1;
            Q1=makeQuery(id+"F1.opExtrude","SWEPT_EDGE",EDGE,{"disambiguationData":[OSD([sQuery(id+"F0.wireOp",EDGE,"E7"),sQuery(id+"F0.wireOp",EDGE,"E9"),sQuery(id+"F0.wireOp",EDGE,"E75")])]});
            var Q2;
            Q2=makeQuery(id+"F1.opExtrude","SWEPT_EDGE",EDGE,{"disambiguationData":[OSD([sQuery(id+"F0.wireOp",EDGE,"E30"),sQuery(id+"F0.wireOp",EDGE,"E33")])]});
            var Q3;
            Q3=makeQuery(id+"F1.opExtrude","SWEPT_EDGE",EDGE,{"disambiguationData":[OSD([sQuery(id+"F0.wireOp",EDGE,"E31"),sQuery(id+"F0.wireOp",EDGE,"E34")])]});
            var Q4;
            Q4=makeQuery(id+"F1.opExtrude","SWEPT_EDGE",EDGE,{"disambiguationData":[OSD([sQuery(id+"F0.wireOp",EDGE,"E28"),sQuery(id+"F0.wireOp",EDGE,"E32")])]});
            var Q5;
            Q5=makeQuery(id+"F1.opExtrude","SWEPT_EDGE",EDGE,{"disambiguationData":[OSD([sQuery(id+"F0.wireOp",EDGE,"E26"),sQuery(id+"F0.wireOp",EDGE,"E38")])]});
            fillet(context, id + "F4", {"entities" : qUnion([Q0, Q1, Q2, Q3, Q4, Q5]), "radius" : 2 * mm, "tangentPropagation" : true, "allowEdgeOverflow" : false});
        }
        {
            var Q0;
            Q0=makeQuery(id+"F1.opExtrude","SWEPT_EDGE",EDGE,{"disambiguationData":[OSD([sQuery(id+"F0.wireOp",EDGE,"E25"),sQuery(id+"F0.wireOp",EDGE,"E32")])]});
            var Q1;
            Q1=makeQuery(id+"F1.opExtrude","SWEPT_EDGE",EDGE,{"disambiguationData":[OSD([sQuery(id+"F0.wireOp",EDGE,"E24"),sQuery(id+"F0.wireOp",EDGE,"E37")])]});
            var Q2;
            Q2=makeQuery(id+"F1.opExtrude","SWEPT_EDGE",EDGE,{"disambiguationData":[OSD([sQuery(id+"F0.wireOp",EDGE,"E37"),sQuery(id+"F0.wireOp",EDGE,"E42")])]});
            var Q3;
            Q3=makeQuery(id+"F1.opExtrude","SWEPT_EDGE",EDGE,{"disambiguationData":[OSD([sQuery(id+"F0.wireOp",EDGE,"E32"),sQuery(id+"F0.wireOp",EDGE,"E44")])]});
            var Q4;
            Q4=makeQuery(id+"F1.opExtrude","SWEPT_EDGE",EDGE,{"disambiguationData":[OSD([sQuery(id+"F0.wireOp",EDGE,"E26"),sQuery(id+"F0.wireOp",EDGE,"E39")])]});
            var Q5;
            Q5=makeQuery(id+"F1.opExtrude","SWEPT_EDGE",EDGE,{"disambiguationData":[OSD([sQuery(id+"F0.wireOp",EDGE,"E40"),sQuery(id+"F0.wireOp",EDGE,"E42")])]});
            var Q6;
            Q6=makeQuery(id+"F1.opExtrude","SWEPT_EDGE",EDGE,{"disambiguationData":[OSD([sQuery(id+"F0.wireOp",EDGE,"E24"),sQuery(id+"F0.wireOp",EDGE,"E40")])]});
            var Q7;
            Q7=makeQuery(id+"F1.opExtrude","SWEPT_EDGE",EDGE,{"disambiguationData":[OSD([sQuery(id+"F0.wireOp",EDGE,"E39"),sQuery(id+"F0.wireOp",EDGE,"E41")])]});
            var Q8;
            Q8=makeQuery(id+"F1.opExtrude","SWEPT_EDGE",EDGE,{"disambiguationData":[OSD([sQuery(id+"F0.wireOp",EDGE,"E43"),sQuery(id+"F0.wireOp",EDGE,"E46")])]});
            var Q9;
            Q9=makeQuery(id+"F1.opExtrude","SWEPT_EDGE",EDGE,{"disambiguationData":[OSD([sQuery(id+"F0.wireOp",EDGE,"E25"),sQuery(id+"F0.wireOp",EDGE,"E45")])]});
            var Q10;
            Q10=makeQuery(id+"F1.opExtrude","SWEPT_EDGE",EDGE,{"disambiguationData":[OSD([sQuery(id+"F0.wireOp",EDGE,"E44"),sQuery(id+"F0.wireOp",EDGE,"E45")])]});
            var Q11;
            Q11=makeQuery(id+"F1.opExtrude","SWEPT_EDGE",EDGE,{"disambiguationData":[OSD([sQuery(id+"F0.wireOp",EDGE,"E28"),sQuery(id+"F0.wireOp",EDGE,"E46")])]});
            var Q12;
            Q12=makeQuery(id+"F1.opExtrude","SWEPT_EDGE",EDGE,{"disambiguationData":[OSD([sQuery(id+"F0.wireOp",EDGE,"E15"),sQuery(id+"F0.wireOp",EDGE,"E31")])]});
            var Q13;
            Q13=makeQuery(id+"F1.opExtrude","SWEPT_EDGE",EDGE,{"disambiguationData":[OSD([sQuery(id+"F0.wireOp",EDGE,"E15"),sQuery(id+"F0.wireOp",EDGE,"E30")])]});
            var Q14;
            Q14=makeQuery(id+"F1.opExtrude","SWEPT_EDGE",EDGE,{"disambiguationData":[OSD([sQuery(id+"F0.wireOp",EDGE,"E17"),sQuery(id+"F0.wireOp",EDGE,"E33")])]});
            var Q15;
            Q15=makeQuery(id+"F1.opExtrude","SWEPT_EDGE",EDGE,{"disambiguationData":[OSD([sQuery(id+"F0.wireOp",EDGE,"E18"),sQuery(id+"F0.wireOp",EDGE,"E34")])]});
            var Q16;
            Q16=makeQuery(id+"F1.opExtrude","SWEPT_EDGE",EDGE,{"disambiguationData":[OSD([sQuery(id+"F0.wireOp",EDGE,"E47"),sQuery(id+"F0.wireOp",EDGE,"E51")])]});
            var Q17;
            Q17=makeQuery(id+"F1.opExtrude","SWEPT_EDGE",EDGE,{"disambiguationData":[OSD([sQuery(id+"F0.wireOp",EDGE,"E35"),sQuery(id+"F0.wireOp",EDGE,"E48")])]});
            var Q18;
            Q18=makeQuery(id+"F1.opExtrude","SWEPT_EDGE",EDGE,{"disambiguationData":[OSD([sQuery(id+"F0.wireOp",EDGE,"E53"),sQuery(id+"F0.wireOp",EDGE,"E55")])]});
            var Q19;
            Q19=makeQuery(id+"F1.opExtrude","SWEPT_EDGE",EDGE,{"disambiguationData":[OSD([sQuery(id+"F0.wireOp",EDGE,"E36"),sQuery(id+"F0.wireOp",EDGE,"E56")])]});
            var Q20;
            Q20=makeQuery(id+"F1.opExtrude","SWEPT_EDGE",EDGE,{"disambiguationData":[OSD([sQuery(id+"F0.wireOp",EDGE,"E53"),sQuery(id+"F0.wireOp",EDGE,"E58")])]});
            var Q21;
            Q21=makeQuery(id+"F1.opExtrude","SWEPT_EDGE",EDGE,{"disambiguationData":[OSD([sQuery(id+"F0.wireOp",EDGE,"E36"),sQuery(id+"F0.wireOp",EDGE,"E57")])]});
            var Q22;
            Q22=makeQuery(id+"F1.opExtrude","SWEPT_EDGE",EDGE,{"disambiguationData":[OSD([sQuery(id+"F0.wireOp",EDGE,"E35"),sQuery(id+"F0.wireOp",EDGE,"E49")])]});
            var Q23;
            Q23=makeQuery(id+"F1.opExtrude","SWEPT_EDGE",EDGE,{"disambiguationData":[OSD([sQuery(id+"F0.wireOp",EDGE,"E50"),sQuery(id+"F0.wireOp",EDGE,"E51")])]});
            var Q24;
            Q24=makeQuery(id+"F1.opExtrude","SWEPT_EDGE",EDGE,{"disambiguationData":[OSD([sQuery(id+"F0.wireOp",EDGE,"E48"),sQuery(id+"F0.wireOp",EDGE,"E52")])]});
            var Q25;
            Q25=makeQuery(id+"F1.opExtrude","SWEPT_EDGE",EDGE,{"disambiguationData":[OSD([sQuery(id+"F0.wireOp",EDGE,"E27"),sQuery(id+"F0.wireOp",EDGE,"E47")])]});
            var Q26;
            Q26=makeQuery(id+"F1.opExtrude","SWEPT_EDGE",EDGE,{"disambiguationData":[OSD([sQuery(id+"F0.wireOp",EDGE,"E29"),sQuery(id+"F0.wireOp",EDGE,"E55")])]});
            var Q27;
            Q27=makeQuery(id+"F1.opExtrude","SWEPT_EDGE",EDGE,{"disambiguationData":[OSD([sQuery(id+"F0.wireOp",EDGE,"E54"),sQuery(id+"F0.wireOp",EDGE,"E56")])]});
            var Q28;
            Q28=makeQuery(id+"F1.opExtrude","SWEPT_EDGE",EDGE,{"disambiguationData":[OSD([sQuery(id+"F0.wireOp",EDGE,"E49"),sQuery(id+"F0.wireOp",EDGE,"E52")])]});
            var Q29;
            Q29=makeQuery(id+"F1.opExtrude","SWEPT_EDGE",EDGE,{"disambiguationData":[OSD([sQuery(id+"F0.wireOp",EDGE,"E27"),sQuery(id+"F0.wireOp",EDGE,"E50")])]});
            var Q30;
            Q30=makeQuery(id+"F1.opExtrude","SWEPT_EDGE",EDGE,{"disambiguationData":[OSD([sQuery(id+"F0.wireOp",EDGE,"E29"),sQuery(id+"F0.wireOp",EDGE,"E58")])]});
            var Q31;
            Q31=makeQuery(id+"F1.opExtrude","SWEPT_EDGE",EDGE,{"disambiguationData":[OSD([sQuery(id+"F0.wireOp",EDGE,"E54"),sQuery(id+"F0.wireOp",EDGE,"E57")])]});
            var Q32;
            Q32=makeQuery(id+"F1.opExtrude","SWEPT_EDGE",EDGE,{"disambiguationData":[OSD([sQuery(id+"F0.wireOp",EDGE,"E76"),sQuery(id+"F0.wireOp",EDGE,"E78")])]});
            var Q33;
            Q33=makeQuery(id+"F1.opExtrude","SWEPT_EDGE",EDGE,{"disambiguationData":[OSD([sQuery(id+"F0.wireOp",EDGE,"E79"),sQuery(id+"F0.wireOp",EDGE,"E82")])]});
            var Q34;
            Q34=makeQuery(id+"F1.opExtrude","SWEPT_EDGE",EDGE,{"disambiguationData":[OSD([sQuery(id+"F0.wireOp",EDGE,"E80"),sQuery(id+"F0.wireOp",EDGE,"E89")])]});
            var Q35;
            Q35=makeQuery(id+"F1.opExtrude","SWEPT_EDGE",EDGE,{"disambiguationData":[OSD([sQuery(id+"F0.wireOp",EDGE,"E83"),sQuery(id+"F0.wireOp",EDGE,"E87")])]});
            var Q36;
            Q36=makeQuery(id+"F1.opExtrude","SWEPT_EDGE",EDGE,{"disambiguationData":[OSD([sQuery(id+"F0.wireOp",EDGE,"E76"),sQuery(id+"F0.wireOp",EDGE,"E88")])]});
            var Q37;
            Q37=makeQuery(id+"F1.opExtrude","SWEPT_EDGE",EDGE,{"disambiguationData":[OSD([sQuery(id+"F0.wireOp",EDGE,"E82"),sQuery(id+"F0.wireOp",EDGE,"E86")])]});
            var Q38;
            Q38=makeQuery(id+"F1.opExtrude","SWEPT_EDGE",EDGE,{"disambiguationData":[OSD([sQuery(id+"F0.wireOp",EDGE,"E80"),sQuery(id+"F0.wireOp",EDGE,"E84")])]});
            var Q39;
            Q39=makeQuery(id+"F1.opExtrude","SWEPT_EDGE",EDGE,{"disambiguationData":[OSD([sQuery(id+"F0.wireOp",EDGE,"E83"),sQuery(id+"F0.wireOp",EDGE,"E85")])]});
            var Q40;
            Q40=makeQuery(id+"F1.opExtrude","SWEPT_EDGE",EDGE,{"disambiguationData":[OSD([sQuery(id+"F0.wireOp",EDGE,"E77"),sQuery(id+"F0.wireOp",EDGE,"E79")])]});
            var Q41;
            Q41=makeQuery(id+"F1.opExtrude","SWEPT_EDGE",EDGE,{"disambiguationData":[OSD([sQuery(id+"F0.wireOp",EDGE,"E78"),sQuery(id+"F0.wireOp",EDGE,"E90")])]});
            var Q42;
            Q42=makeQuery(id+"F1.opExtrude","SWEPT_EDGE",EDGE,{"disambiguationData":[OSD([sQuery(id+"F0.wireOp",EDGE,"E89"),sQuery(id+"F0.wireOp",EDGE,"E91")])]});
            var Q43;
            Q43=makeQuery(id+"F1.opExtrude","SWEPT_EDGE",EDGE,{"disambiguationData":[OSD([sQuery(id+"F0.wireOp",EDGE,"E81"),sQuery(id+"F0.wireOp",EDGE,"E87")])]});
            var Q44;
            Q44=makeQuery(id+"F1.opExtrude","SWEPT_EDGE",EDGE,{"disambiguationData":[OSD([sQuery(id+"F0.wireOp",EDGE,"E77"),sQuery(id+"F0.wireOp",EDGE,"E86")])]});
            var Q45;
            Q45=makeQuery(id+"F1.opExtrude","SWEPT_EDGE",EDGE,{"disambiguationData":[OSD([sQuery(id+"F0.wireOp",EDGE,"E88"),sQuery(id+"F0.wireOp",EDGE,"E90")])]});
            var Q46;
            Q46=makeQuery(id+"F1.opExtrude","SWEPT_EDGE",EDGE,{"disambiguationData":[OSD([sQuery(id+"F0.wireOp",EDGE,"E84"),sQuery(id+"F0.wireOp",EDGE,"E91")])]});
            var Q47;
            Q47=makeQuery(id+"F1.opExtrude","SWEPT_EDGE",EDGE,{"disambiguationData":[OSD([sQuery(id+"F0.wireOp",EDGE,"E81"),sQuery(id+"F0.wireOp",EDGE,"E85")])]});
            fillet(context, id + "F5", {"entities" : qUnion([Q0, Q1, Q2, Q3, Q4, Q5, Q6, Q7, Q8, Q9, Q10, Q11, Q12, Q13, Q14, Q15, Q16, Q17, Q18, Q19, Q20, Q21, Q22, Q23, Q24, Q25, Q26, Q27, Q28, Q29, Q30, Q31, Q32, Q33, Q34, Q35, Q36, Q37, Q38, Q39, Q40, Q41, Q42, Q43, Q44, Q45, Q46, Q47]), "radius" : 2 * mm, "tangentPropagation" : true, "allowEdgeOverflow" : false});
        }
    });
